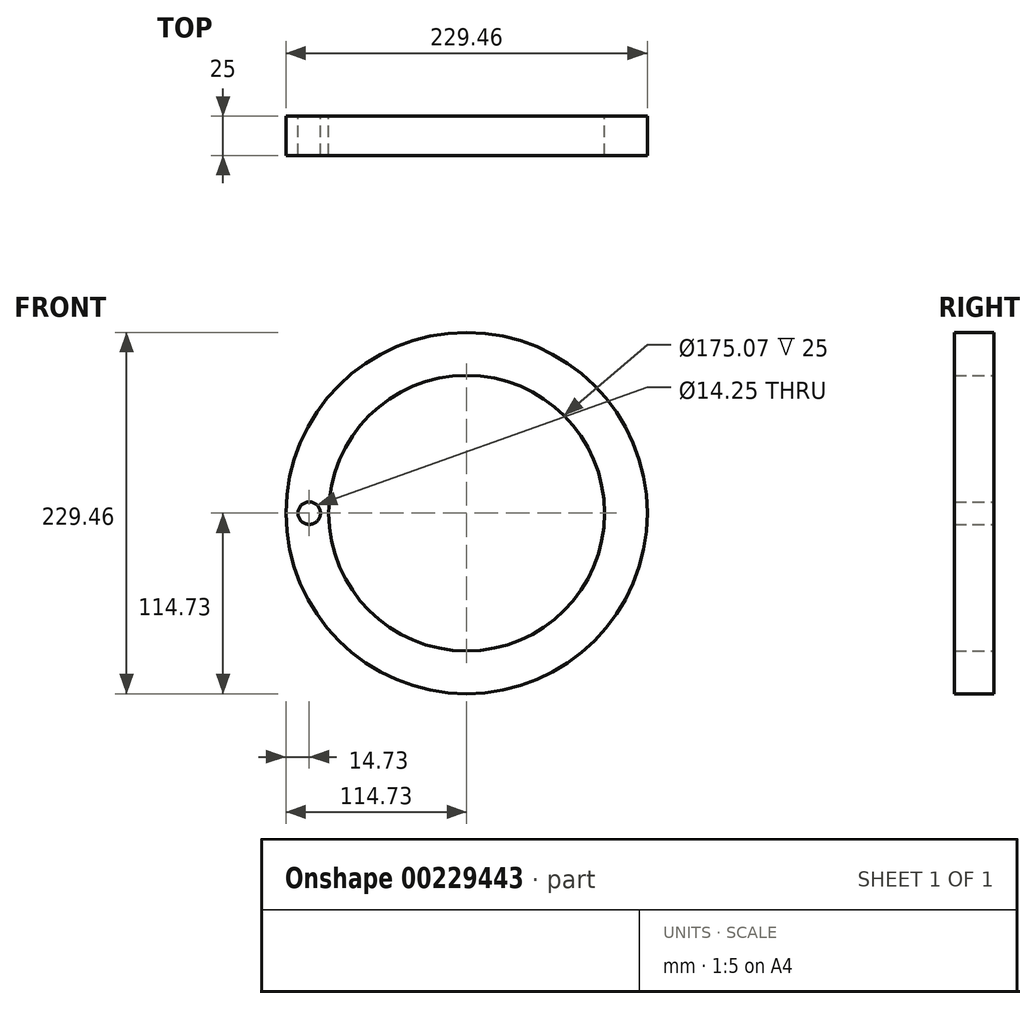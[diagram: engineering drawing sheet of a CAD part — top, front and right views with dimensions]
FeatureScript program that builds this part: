
annotation { "Feature Type Name" : "Feature", "Feature Type Description" : "" }
export const myFeature = defineFeature(function(context is Context, id is Id, definition is map)
    precondition{}
    {
        {
            var Q0;
            Q0=qCreatedBy(makeId("Front.planeOp"),FACE);
            var sketch = newSketch(context, id + "F0", { "sketchPlane" : qUnion([Q0])});
            skCircle(sketch, "E0", {"center": v(0, 0) * mm, "radius": 100 * mm, "construction": true});
            skCircle(sketch, "E1", {"center": v(0, 0) * mm, "radius": 114.73 * mm});
            skCircle(sketch, "E2", {"center": v(0, 0) * mm, "radius": 87.54 * mm});
            skCircle(sketch, "E3", {"center": v(-100, 0) * mm, "radius": 7.13 * mm});
            skSolve(sketch);
        }
        {
            var Q0;
            Q0=makeQuery(id+"F0.imprint","IMPRINT",FACE,{"disambiguationData":[TD([[makeQuery(id+"F0.imprint","IMPRINT",EDGE,{"derivedFrom":sQuery(id+"F0.wireOp",EDGE,"E1")}),1.0]])]});
            extrude(context, id + "F1", {"entities" : qUnion([Q0]), "depth" : 25 * mm});
        }
    });
